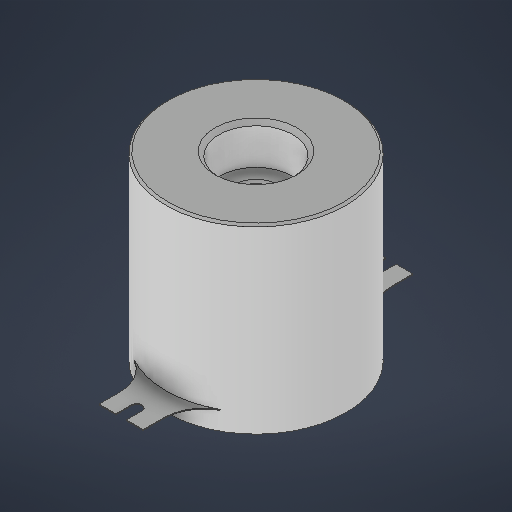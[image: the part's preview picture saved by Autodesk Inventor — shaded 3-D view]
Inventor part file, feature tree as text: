
AUTODESK INVENTOR PART (.ipt)
format: ipt  version: 2025 (Build 290162000, 162)  size: 282,624 bytes
history: native  units: mm
features: sketch x12, plane x5, loft x5, hole x3, other x3, extrude x2, chamfer x2
ambient origin geometry x8: Origin, YZ Plane, XZ Plane, XY Plane, X Axis, Y Axis, Z Axis, Center Point
bodies: Solid1 (feature_tree)
feature tree (32):
  sketch  "Sketch1"  dims[d0=44.8mm d1=40.5mm]
  plane  "Work Plane1"
  sketch  "Sketch2"  dims[d2=-81.5mm d3=-12.0mm d4=67.6mm]
  plane  "Work Plane3"
  sketch  "Sketch3"  dims[d5=0.0mm d6=90.0deg d7=0.0mm d8=90.0deg]
  sketch  "Sketch4"  dims[d13=0.0mm d14=90.0deg d15=0.0mm d16=90.0deg]
  loft  "Loft1"
  loft  "Loft3"
  extrude  "Extrusion1"  TaperAngle=0.0deg  [1 undecoded]
  plane  "Work Plane4"
  sketch  "Sketch6"  dims[d19=10.0mm d20=2.6mm]
  plane  "Work Plane5"
  loft  "Loft4"
  loft  "Loft5"
  loft  "Loft6"
  hole  "Hole1"  [1 undecoded]
  chamfer  "Chamfer1"  Distance=0.2mm
  chamfer  "Chamfer2"  Angle=90.0deg  [1 undecoded]
  hole  "Hole2"  [1 undecoded]
  extrude  "Extrusion2"  TaperAngle=0.0deg  [1 undecoded]
  hole  "Hole3"  [1 undecoded]
  plane  "Work Plane2"
  other  "Edges2"
  sketch  "Sketch5"  dims[d17=11.0mm d18=67.2mm]
  sketch  "Sketch7"  dims[d21=5.2mm d22=1.3mm d23=0.2mm d24=0.0mm]
  other  "Edges3"
  sketch  "Sketch8"  dims[d25=-4.7mm]
  other  "Edges4"
  sketch  "Sketch9"  dims[d26=-93.5mm d27=0.0mm d28=90.0deg]
  sketch  "Sketch10"  dims[d29=0.0mm d30=90.0deg d31=0.0mm d32=90.0deg]
  sketch  "Sketch11"  dims[d33=0.0mm d34=90.0deg d35=0.0mm d36=90.0deg]
  sketch  "Sketch12"  dims[d37=0.0mm d38=90.0deg d39=18.4mm d40=6.0mm d41=4.0mm d42=2.0mm d43=90.0deg d44=10.0mm d45=0.0mm d46=1.0mm d47=2.0mm d48=45.0deg d49=0.5mm d50=2.0mm d51=45.0deg d52=13.5mm d53=6.0mm d54=4.0mm d55=2.0mm d56=90.0deg d57=10.0mm d58=0.0mm d59=48.3mm d60=0.0mm d61=10.106mm d62=40.0mm d63=11.2mm d64=2.0mm d65=90.0deg d66=10.0mm d67=0.0mm]
note: 6 required parameter values undecoded (feature->parameter linkage not recoverable at this tier; creation-order binding heuristic only, values carry confidence <= 0.55)
